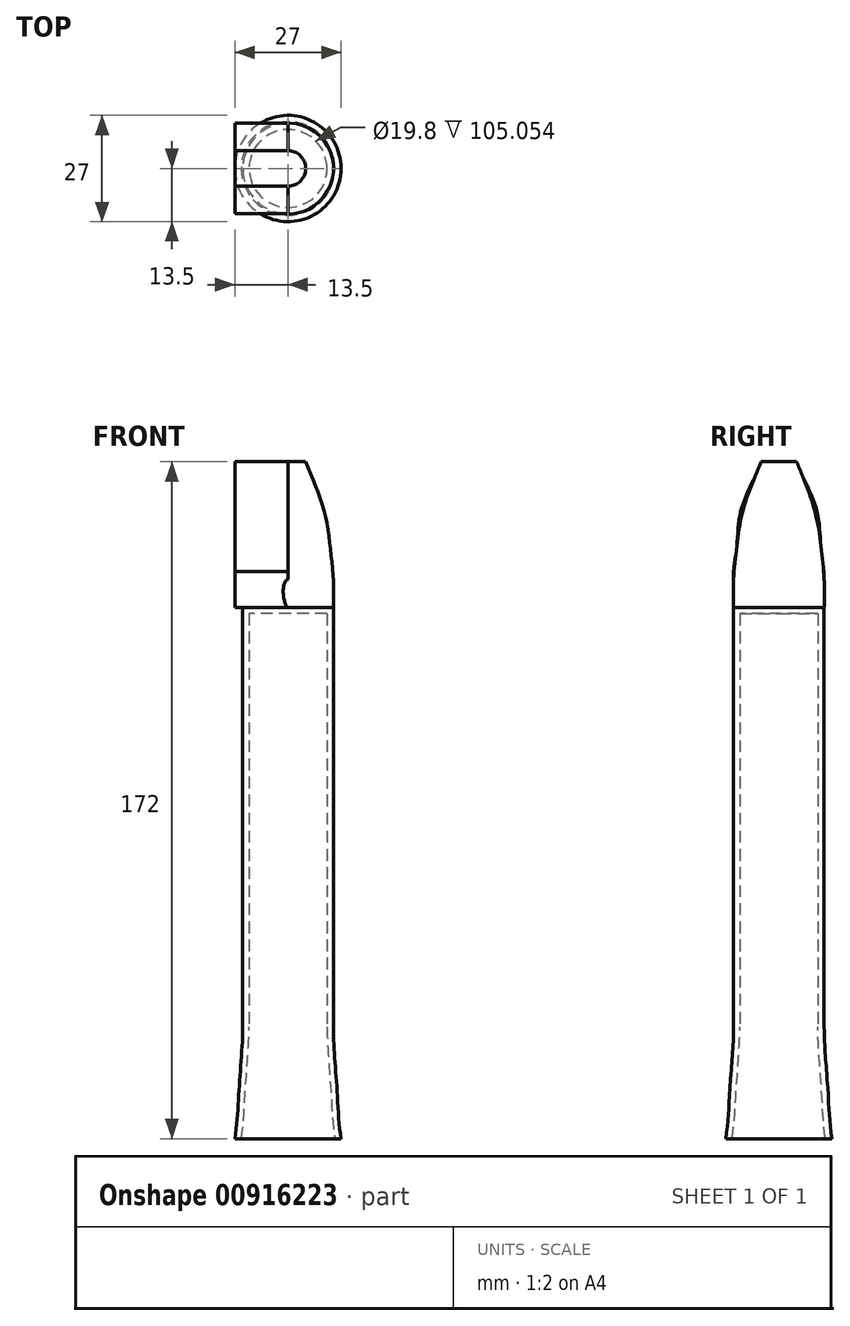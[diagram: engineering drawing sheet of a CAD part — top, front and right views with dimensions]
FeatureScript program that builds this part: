
annotation { "Feature Type Name" : "Feature", "Feature Type Description" : "" }
export const myFeature = defineFeature(function(context is Context, id is Id, definition is map)
    precondition{}
    {
        {
            var Q0;
            Q0=qCreatedBy(makeId("Top.planeOp"),FACE);
            var sketch = newSketch(context, id + "F0", { "sketchPlane" : qUnion([Q0])});
            skCircle(sketch, "E0", {"center": v(0, 0) * mm, "radius": 11.5 * mm});
            skSolve(sketch);
        }
        {
            var Q0;
            Q0=makeQuery(id+"F0.imprint","IMPRINT",FACE,{"disambiguationData":[TD([[makeQuery(id+"F0.imprint","IMPRINT",EDGE,{"derivedFrom":sQuery(id+"F0.wireOp",EDGE,"E0")}),1.0]])]});
            extrude(context, id + "F1", {"entities" : qUnion([Q0]), "depth" : 135 * mm, "offsetDistance" : 25 * mm});
        }
        {
            var Q0;
            Q0=qCreatedBy(makeId("Front.planeOp"),FACE);
            var sketch = newSketch(context, id + "F2", { "sketchPlane" : qUnion([Q0])});
            skLineSegment(sketch, "E1", {"start": v(0, 0) * mm, "end": v(0, 28.35) * mm, "construction": true});
            skLineSegment(sketch, "E2", {"start": v(0, 28.35) * mm, "end": v(-11.5, 28.35) * mm, "construction": true});
            skFitSpline(sketch, "E3", {"points": [v(-11.5, 28.35) * mm, v(-11.86, 20.54) * mm, v(-12.52, 11.23) * mm, v(-13.5, 0) * mm], "startDerivative": vector(-0.13, -24.63) * mm, "endDerivative": vector(-5, -27.65) * mm});
            skLineSegment(sketch, "E4", {"start": v(-13.5, 0) * mm, "end": v(0, 0) * mm});
            skLineSegment(sketch, "E5", {"start": v(0, 28.35) * mm, "end": v(-11.5, 28.35) * mm});
            skLineSegment(sketch, "E6", {"start": v(0, 28.35) * mm, "end": v(0, 0) * mm});
            skSolve(sketch);
        }
        {
            var Q0;
            Q0 = qSketchRegion(id + "F2", true);
            var Q1;
            Q1=sQuery(id+"F2.wireOp",EDGE,"E6");
            revolve(context, id + "F3", {"operationType" : NewBodyOperationType.ADD, "surfaceOperationType" : NewSurfaceOperationType.NEW, "entities" : qUnion([Q0]), "axis" : qUnion([Q1]), "revolveType" : RevolveType.FULL});
        }
        {
            var Q0;
            Q0=makeQuery(id+"F3.boolean.opBoolean","MERGE",FACE,{"derivedFrom":[makeQuery(id+"F1.opExtrude","CAP_FACE",FACE,{"disambiguationData":[OSD([sQuery(id+"F0.wireOp",EDGE,"E0")])],"isStart":true}),makeQuery(id+"F3.opRevolve","SWEPT_FACE",FACE,{"disambiguationData":[OSD([sQuery(id+"F2.wireOp",EDGE,"E4")])]})]});
            var Q1;
            Q1=makeQuery(id+"F1.opExtrude","SWEPT_BODY",BODY,{"disambiguationData":[OSD([sQuery(id+"F0.wireOp",EDGE,"E0")])]});
            shell(context, id + "F4", {"entities" : qUnion([Q0]), "parts" : qUnion([Q1]), "thickness" : 1.6 * mm});
        }
        {
            var Q0;
            Q0=qCreatedBy(makeId("Front.planeOp"),FACE);
            var sketch = newSketch(context, id + "F5", { "sketchPlane" : qUnion([Q0])});
            skLineSegment(sketch, "E7", {"start": v(0, 135) * mm, "end": v(0, 172) * mm, "construction": true});
            skLineSegment(sketch, "E8", {"start": v(0, 172) * mm, "end": v(4.5, 172) * mm});
            skLineSegment(sketch, "E9.0", {"start": v(0, 135) * mm, "end": v(11.5, 135) * mm});
            skFitSpline(sketch, "E10", {"points": [v(11.5, 135) * mm, v(11.5, 142) * mm, v(10.72, 150.35) * mm, v(9.13, 159.59) * mm, v(4.5, 172) * mm], "startDerivative": vector(0.77, 31.72) * mm, "endDerivative": vector(-18.04, 43.08) * mm});
            skPoint(sketch, "E11.orphan", {"position": v(0, 114.74) * mm});
            skPoint(sketch, "E12.orphan", {"position": v(-11.5, 135) * mm});
            skLineSegment(sketch, "E13", {"start": v(0, 172) * mm, "end": v(0, 135) * mm});
            skSolve(sketch);
        }
        {
            var Q0;
            Q0 = qSketchRegion(id + "F5", true);
            var Q1;
            Q1=sQuery(id+"F5.wireOp",EDGE,"E13");
            revolve(context, id + "F6", {"operationType" : NewBodyOperationType.ADD, "surfaceOperationType" : NewSurfaceOperationType.NEW, "entities" : qUnion([Q0]), "axis" : qUnion([Q1]), "revolveType" : RevolveType.FULL});
        }
        {
            var Q0;
            Q0=qCreatedBy(makeId("Front.planeOp"),FACE);
            var sketch = newSketch(context, id + "F7", { "sketchPlane" : qUnion([Q0])});
            skLineSegment(sketch, "E14.0", {"start": v(-4.5, 172) * mm, "end": v(0, 172) * mm});
            skLineSegment(sketch, "E15", {"start": v(-4.5, 172) * mm, "end": v(-13.5, 172) * mm});
            skLineSegment(sketch, "E16", {"start": v(-13.5, 172) * mm, "end": v(-13.5, 135) * mm});
            skLineSegment(sketch, "E17", {"start": v(0, 172) * mm, "end": v(0, 135) * mm, "construction": true});
            skLineSegment(sketch, "E18", {"start": v(-13.5, 135) * mm, "end": v(0, 135) * mm});
            skLineSegment(sketch, "E19", {"start": v(0, 172) * mm, "end": v(0, 133.74) * mm});
            skPoint(sketch, "E20.orphan", {"position": v(4.5, 172) * mm});
            skSolve(sketch);
        }
        {
            var Q0;
            Q0 = qSketchRegion(id + "F7", true);
            extrude(context, id + "F8", {"entities" : qUnion([Q0]), "operationType" : NewBodyOperationType.ADD, "endBound" : BoundingType.SYMMETRIC, "depth" : 23 * mm, "offsetDistance" : 25 * mm});
        }
        {
            var Q0;
            Q0=qCreatedBy(makeId("Right.planeOp"),FACE);
            var sketch = newSketch(context, id + "F9", { "sketchPlane" : qUnion([Q0])});
            skFitSpline(sketch, "E21.0", {"points": [v(-4.5, 172) * mm, v(-6.29, 167.73) * mm, v(-9.58, 159.87) * mm, v(-10.71, 150.53) * mm, v(-11.67, 142.07) * mm, v(-11.56, 137.29) * mm, v(-11.5, 135) * mm]});
            skFitSpline(sketch, "E21.1", {"points": [v(11.5, 135) * mm, v(11.56, 137.29) * mm, v(11.67, 142.07) * mm, v(10.71, 150.53) * mm, v(9.58, 159.87) * mm, v(6.29, 167.73) * mm, v(4.5, 172) * mm]});
            skLineSegment(sketch, "E22", {"start": v(4.5, 172) * mm, "end": v(13.5, 172) * mm});
            skLineSegment(sketch, "E23", {"start": v(13.5, 172) * mm, "end": v(11.5, 142) * mm});
            skLineSegment(sketch, "E24", {"start": v(-4.5, 172) * mm, "end": v(-14.2, 172) * mm});
            skLineSegment(sketch, "E25", {"start": v(-14.2, 172) * mm, "end": v(-11.5, 142) * mm});
            skSolve(sketch);
        }
        {
            var Q0;
            Q0 = qSketchRegion(id + "F9", true);
            extrude(context, id + "F10", {"entities" : qUnion([Q0]), "operationType" : NewBodyOperationType.REMOVE, "oppositeDirection" : true, "depth" : 25 * mm, "offsetDistance" : 25 * mm});
        }
    });
